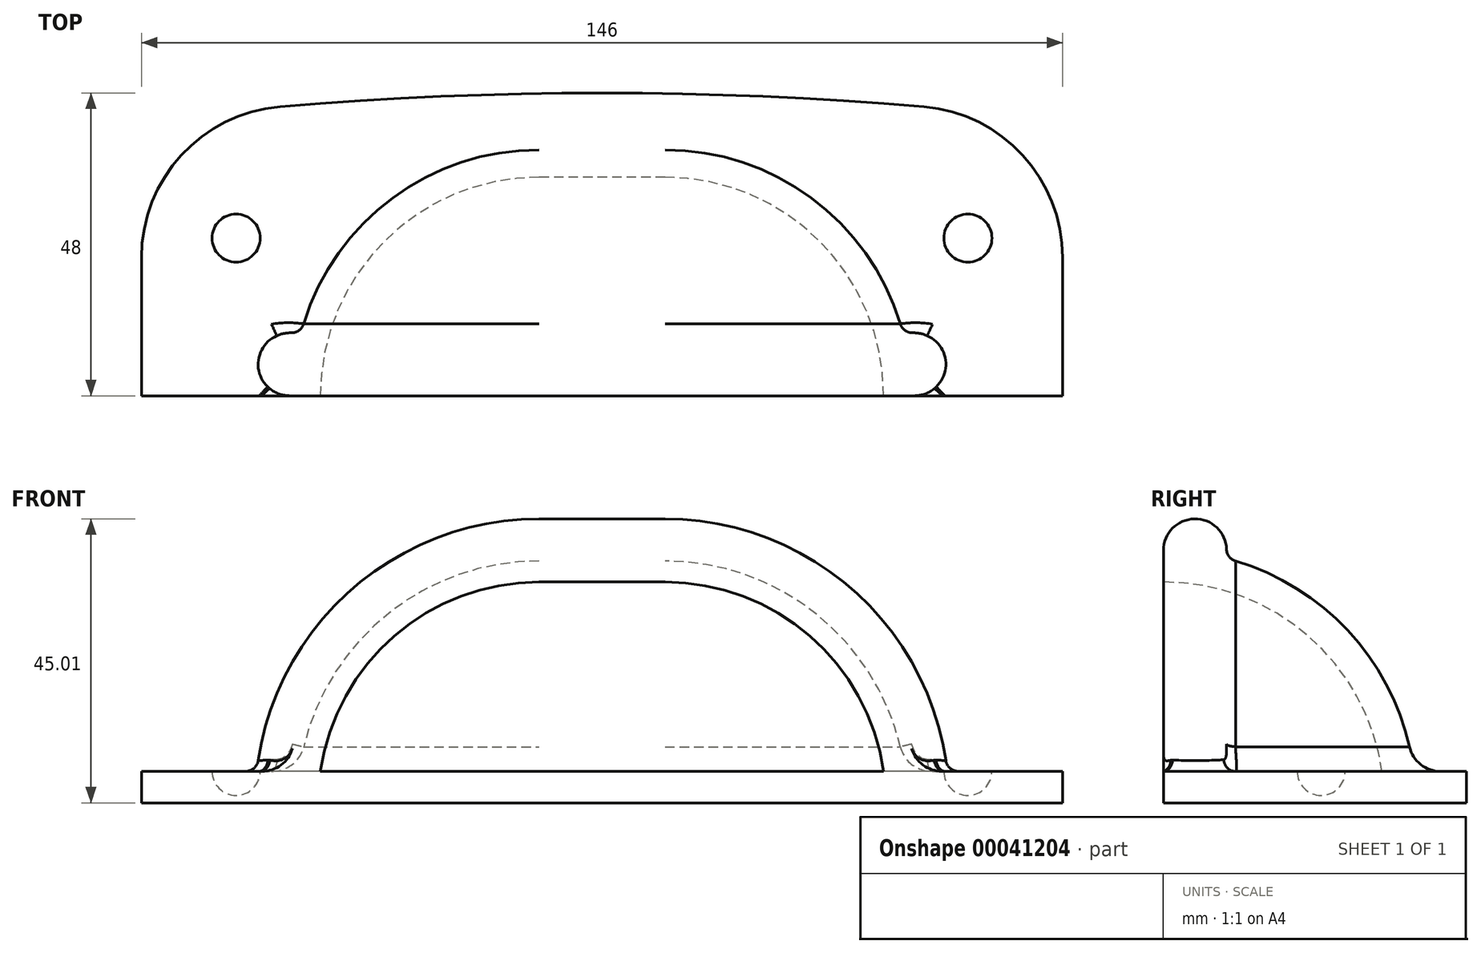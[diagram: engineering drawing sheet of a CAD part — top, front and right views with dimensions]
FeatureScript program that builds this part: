
annotation { "Feature Type Name" : "Feature", "Feature Type Description" : "" }
export const myFeature = defineFeature(function(context is Context, id is Id, definition is map)
    precondition{}
    {
        {
            var Q0;
            Q0=qCreatedBy(makeId("Top.planeOp"),FACE);
            var sketch = newSketch(context, id + "F0", { "sketchPlane" : qUnion([Q0])});
            skLineSegment(sketch, "E0", {"start": v(0, 0) * mm, "end": v(10, 0) * mm, "construction": true});
            skArc(sketch, "E1", {"start": v(10, 35) * mm, "mid": v(34.75, 24.75) * mm, "end": v(45, 0) * mm});
            skLineSegment(sketch, "E2", {"start": v(10, 35) * mm, "end": v(0, 35) * mm});
            skLineSegment(sketch, "E3", {"start": v(45, 0) * mm, "end": v(50, 0) * mm});
            skLineSegment(sketch, "E4.0", {"start": v(10, 40) * mm, "end": v(0, 40) * mm});
            skArc(sketch, "E4.1", {"start": v(10, 40) * mm, "mid": v(38.28, 28.28) * mm, "end": v(50, 0) * mm});
            skLineSegment(sketch, "E5", {"start": v(0, 40) * mm, "end": v(0, 0) * mm, "construction": true});
            skLineSegment(sketch, "E6.MirrorCS", {"start": v(-10, 35) * mm, "end": v(0, 35) * mm});
            skArc(sketch, "E7.MirrorCS", {"start": v(-10, 35) * mm, "mid": v(-34.75, 24.75) * mm, "end": v(-45, 0) * mm});
            skLineSegment(sketch, "E8.MirrorCS", {"start": v(-45, 0) * mm, "end": v(-50, 0) * mm});
            skArc(sketch, "E9.MirrorCS", {"start": v(-10, 40) * mm, "mid": v(-38.28, 28.28) * mm, "end": v(-50, 0) * mm});
            skLineSegment(sketch, "E10.MirrorCS", {"start": v(-10, 40) * mm, "end": v(0, 40) * mm});
            skLineSegment(sketch, "E11.MirrorCS", {"start": v(0, 0) * mm, "end": v(-10, 0) * mm});
            skSolve(sketch);
        }
        {
            var Q0;
            Q0 = qSketchRegion(id + "F0", true);
            var Q1;
            Q1=sQuery(id+"F0.wireOp",EDGE,"E0");
            revolve(context, id + "F1", {"entities" : qUnion([Q0]), "axis" : qUnion([Q1]), "revolveType" : RevolveType.ONE_DIRECTION, "angle" : 90 * degree});
        }
        {
            var Q0;
            Q0=qCreatedBy(makeId("Top.planeOp"),FACE);
            var sketch = newSketch(context, id + "F2", { "sketchPlane" : qUnion([Q0])});
            skArc(sketch, "E12", {"start": v(51.04, 45.83) * mm, "mid": v(25.54, 47.46) * mm, "end": v(0, 48) * mm});
            skLineSegment(sketch, "E13", {"start": v(0, 0) * mm, "end": v(0, 48) * mm, "construction": true});
            skLineSegment(sketch, "E14", {"start": v(0, 48) * mm, "end": v(-79.99, 48) * mm, "construction": true});
            skLineSegment(sketch, "E15", {"start": v(0, 0) * mm, "end": v(10, 0) * mm});
            skLineSegment(sketch, "E16", {"start": v(73, 0) * mm, "end": v(73, 21.91) * mm});
            skPoint(sketch, "E17.visualSharp", {"position": v(73, 43.54) * mm});
            skArc(sketch, "E17.filletArc", {"start": v(73, 21.91) * mm, "mid": v(66.68, 38.14) * mm, "end": v(51.04, 45.83) * mm});
            skArc(sketch, "E18.MirrorCS", {"start": v(-51.04, 45.83) * mm, "mid": v(-25.54, 47.46) * mm, "end": v(0, 48) * mm});
            skArc(sketch, "E19.MirrorCS", {"start": v(-73, 21.91) * mm, "mid": v(-66.68, 38.14) * mm, "end": v(-51.04, 45.83) * mm});
            skLineSegment(sketch, "E20.MirrorCS", {"start": v(-73, 0) * mm, "end": v(-73, 21.91) * mm});
            skLineSegment(sketch, "E21.MirrorCS", {"start": v(0, 0) * mm, "end": v(-10, 0) * mm});
            skArc(sketch, "E22.0", {"start": v(-10, 35) * mm, "mid": v(-34.75, 24.75) * mm, "end": v(-45, 0) * mm});
            skLineSegment(sketch, "E22.1", {"start": v(10, 35) * mm, "end": v(-10, 35) * mm});
            skArc(sketch, "E22.2", {"start": v(10, 35) * mm, "mid": v(34.75, 24.75) * mm, "end": v(45, 0) * mm});
            skLineSegment(sketch, "E23.trimOffspring", {"start": v(-45, 0) * mm, "end": v(-73, 0) * mm});
            skLineSegment(sketch, "E24.trimOffspring", {"start": v(45, 0) * mm, "end": v(73, 0) * mm});
            skSolve(sketch);
        }
        {
            var Q0;
            Q0 = qSketchRegion(id + "F2", true);
            extrude(context, id + "F3", {"entities" : qUnion([Q0]), "operationType" : NewBodyOperationType.ADD, "depth" : 5 * mm});
        }
        {
            var Q0;
            Q0=qCreatedBy(makeId("Right.planeOp"),FACE);
            var sketch = newSketch(context, id + "F4", { "sketchPlane" : qUnion([Q0])});
            skArc(sketch, "E25.0.0", {"start": v(10, 33.54) * mm, "mid": v(5.05, 34.63) * mm, "end": v(0, 35) * mm});
            skArc(sketch, "E25.0.2", {"start": v(0, 35) * mm, "mid": v(5.05, 34.63) * mm, "end": v(10, 33.54) * mm});
            skLineSegment(sketch, "E26", {"start": v(0, 35) * mm, "end": v(0, 40) * mm});
            skArc(sketch, "E27", {"start": v(0, 40) * mm, "mid": v(5, 45) * mm, "end": v(10, 40) * mm});
            skLineSegment(sketch, "E28", {"start": v(10, 40) * mm, "end": v(10, 33.54) * mm});
            skPoint(sketch, "E29.orphan", {"position": v(35, 0) * mm});
            skSolve(sketch);
        }
        {
            var Q0;
            Q0=makeQuery(id+"F3.boolean.opBoolean","MERGE",FACE,{"derivedFrom":[makeQuery(id+"F1.opRevolve","CAP_FACE",FACE,{"disambiguationData":[OSD([sQuery(id+"F0.wireOp",EDGE,"E1"),sQuery(id+"F0.wireOp",EDGE,"E2"),sQuery(id+"F0.wireOp",EDGE,"E3"),sQuery(id+"F0.wireOp",EDGE,"E4.0"),sQuery(id+"F0.wireOp",EDGE,"E4.1"),sQuery(id+"F0.wireOp",EDGE,"E6.MirrorCS"),sQuery(id+"F0.wireOp",EDGE,"E7.MirrorCS"),sQuery(id+"F0.wireOp",EDGE,"E8.MirrorCS"),sQuery(id+"F0.wireOp",EDGE,"E9.MirrorCS"),sQuery(id+"F0.wireOp",EDGE,"E10.MirrorCS")])],"isStart":false}),makeQuery(id+"F3.opExtrude","SWEPT_FACE",FACE,{"disambiguationData":[OSD([sQuery(id+"F2.wireOp",EDGE,"E23.trimOffspring")])]}),makeQuery(id+"F3.opExtrude","SWEPT_FACE",FACE,{"disambiguationData":[OSD([sQuery(id+"F2.wireOp",EDGE,"E24.trimOffspring")])]})]});
            var sketch = newSketch(context, id + "F5", { "sketchPlane" : qUnion([Q0])});
            skLineSegment(sketch, "E30.0", {"start": v(10, 35) * mm, "end": v(0, 35) * mm});
            skArc(sketch, "E30.1", {"start": v(10, 35) * mm, "mid": v(34.75, 24.75) * mm, "end": v(45, 0) * mm});
            skLineSegment(sketch, "E31", {"start": v(0, 0) * mm, "end": v(0, 35) * mm, "construction": true});
            skPoint(sketch, "E32.orphan", {"position": v(-10, 35) * mm});
            skSolve(sketch);
        }
        {
            var Q0;
            Q0 = qSketchRegion(id + "F4", true);
            var Q1;
            Q1 = qConstructionFilter(qBodyType(qCreatedBy(id + "F5" ,EDGE), BodyType.WIRE), ConstructionObject.NO);
            sweep(context, id + "F6", {"profiles" : qUnion([Q0]), "path" : qUnion([Q1])});
        }
        {
            var Q0;
            Q0=makeQuery(id+"F3.boolean.opBoolean","INTERSECT",EDGE,{"derivedFrom":[makeQuery(id+"F1.opRevolve","SWEPT_FACE",FACE,{"disambiguationData":[OSD([sQuery(id+"F0.wireOp",EDGE,"E9.MirrorCS")])]}),makeQuery(id+"F3.opExtrude","CAP_FACE",FACE,{"disambiguationData":[OSD([sQuery(id+"F2.wireOp",EDGE,"E12"),sQuery(id+"F2.wireOp",EDGE,"E15"),sQuery(id+"F2.wireOp",EDGE,"E16"),sQuery(id+"F2.wireOp",EDGE,"E17.filletArc"),sQuery(id+"F2.wireOp",EDGE,"E18.MirrorCS"),sQuery(id+"F2.wireOp",EDGE,"E19.MirrorCS"),sQuery(id+"F2.wireOp",EDGE,"E20.MirrorCS"),sQuery(id+"F2.wireOp",EDGE,"E21.MirrorCS")])],"isStart":false})]});
            fillet(context, id + "F7", {"entities" : qUnion([Q0]), "radius" : 5 * mm, "tangentPropagation" : true, "allowEdgeOverflow" : false});
        }
        {
            var Q0;
            Q0=makeQuery(id+"F6.opSweep","SWEPT_BODY",BODY,{"disambiguationData":[OSD([sQuery(id+"F4.wireOp",EDGE,"E25.0.2"),sQuery(id+"F4.wireOp",EDGE,"E26"),sQuery(id+"F4.wireOp",EDGE,"E27"),sQuery(id+"F4.wireOp",EDGE,"E28"),sQuery(id+"F5.wireOp",EDGE,"E30.1")])]});
            var Q1;
            Q1=qCreatedBy(makeId("Right.planeOp"),FACE);
            mirror(context, id + "F8", {"entities" : qUnion([Q0]), "mirrorPlane" : qUnion([Q1])});
        }
        {
            var Q0;
            Q0=makeQuery(id+"F1.opRevolve","SWEPT_BODY",BODY,{"disambiguationData":[OSD([sQuery(id+"F0.wireOp",EDGE,"E1"),sQuery(id+"F0.wireOp",EDGE,"E2"),sQuery(id+"F0.wireOp",EDGE,"E3"),sQuery(id+"F0.wireOp",EDGE,"E4.0"),sQuery(id+"F0.wireOp",EDGE,"E4.1"),sQuery(id+"F0.wireOp",EDGE,"E6.MirrorCS"),sQuery(id+"F0.wireOp",EDGE,"E7.MirrorCS"),sQuery(id+"F0.wireOp",EDGE,"E8.MirrorCS"),sQuery(id+"F0.wireOp",EDGE,"E9.MirrorCS"),sQuery(id+"F0.wireOp",EDGE,"E10.MirrorCS")])]});
            var Q1;
            Q1=makeQuery(id+"F8.opPattern","COPY",BODY,{"derivedFrom":makeQuery(id+"F6.opSweep","SWEPT_BODY",BODY,{"disambiguationData":[OSD([sQuery(id+"F4.wireOp",EDGE,"E25.0.2"),sQuery(id+"F4.wireOp",EDGE,"E26"),sQuery(id+"F4.wireOp",EDGE,"E27"),sQuery(id+"F4.wireOp",EDGE,"E28"),sQuery(id+"F5.wireOp",EDGE,"E30.1")])]}),"instanceName":"1"});
            var Q2;
            Q2=makeQuery(id+"F6.opSweep","SWEPT_BODY",BODY,{"disambiguationData":[OSD([sQuery(id+"F4.wireOp",EDGE,"E25.0.2"),sQuery(id+"F4.wireOp",EDGE,"E26"),sQuery(id+"F4.wireOp",EDGE,"E27"),sQuery(id+"F4.wireOp",EDGE,"E28"),sQuery(id+"F5.wireOp",EDGE,"E30.1")])]});
            booleanBodies(context, id + "F9", {"operationType" : BooleanOperationType.UNION, "tools" : qUnion([Q0, Q1, Q2])});
        }
        {
            var Q0;
            Q0=makeQuery(id+"F9.opBoolean","INTERSECT",EDGE,{"derivedFrom":[makeQuery(id+"F6.opSweep","SWEPT_FACE",FACE,{"disambiguationData":[OSD([sQuery(id+"F4.wireOp",EDGE,"E28"),sQuery(id+"F5.wireOp",EDGE,"E30.0")])]}),makeQuery(id+"F1.opRevolve","SWEPT_FACE",FACE,{"disambiguationData":[OSD([sQuery(id+"F0.wireOp",EDGE,"E9.MirrorCS")])]})]});
            var Q1;
            {var subQ0=makeQuery(id+"F6.opSweep","SWEPT_EDGE",EDGE,{"disambiguationData":[OSD([sQuery(id+"F4.wireOp",EDGE,"E27"),sQuery(id+"F4.wireOp",EDGE,"E28"),sQuery(id+"F5.wireOp",EDGE,"E30.0")])]});Q1=makeQuery(id+"F9.opBoolean","MERGE",EDGE,{"derivedFrom":[subQ0,makeQuery(id+"F8.opPattern","COPY",EDGE,{"derivedFrom":subQ0,"instanceName":"1"})]});}
            var Q2;
            Q2=makeQuery(id+"F6.opSweep","SWEPT_EDGE",EDGE,{"disambiguationData":[OSD([sQuery(id+"F4.wireOp",EDGE,"E27"),sQuery(id+"F4.wireOp",EDGE,"E28"),sQuery(id+"F5.wireOp",EDGE,"E30.1")])]});
            var Q3;
            Q3=makeQuery(id+"F9.opBoolean","INTERSECT",EDGE,{"derivedFrom":[makeQuery(id+"F7.opFillet","BLEND_FACE",FACE,{"disambiguationData":[OSD([sQuery(id+"F0.wireOp",EDGE,"E9.MirrorCS"),sQuery(id+"F2.wireOp",EDGE,"E12"),sQuery(id+"F2.wireOp",EDGE,"E16"),sQuery(id+"F2.wireOp",EDGE,"E17.filletArc"),sQuery(id+"F2.wireOp",EDGE,"E18.MirrorCS"),sQuery(id+"F2.wireOp",EDGE,"E19.MirrorCS"),sQuery(id+"F2.wireOp",EDGE,"E20.MirrorCS"),sQuery(id+"F2.wireOp",EDGE,"E22.0"),sQuery(id+"F2.wireOp",EDGE,"E22.1"),sQuery(id+"F2.wireOp",EDGE,"E22.2"),sQuery(id+"F2.wireOp",EDGE,"E23.trimOffspring"),sQuery(id+"F2.wireOp",EDGE,"E24.trimOffspring")])]}),makeQuery(id+"F8.opPattern","COPY",FACE,{"derivedFrom":makeQuery(id+"F6.opSweep","SWEPT_FACE",FACE,{"disambiguationData":[OSD([sQuery(id+"F4.wireOp",EDGE,"E27"),sQuery(id+"F5.wireOp",EDGE,"E30.1")])]}),"instanceName":"1"})]});
            var Q4;
            Q4=makeQuery(id+"F8.opPattern","COPY",EDGE,{"derivedFrom":makeQuery(id+"F6.opSweep","SWEPT_EDGE",EDGE,{"disambiguationData":[OSD([sQuery(id+"F4.wireOp",EDGE,"E27"),sQuery(id+"F4.wireOp",EDGE,"E28"),sQuery(id+"F5.wireOp",EDGE,"E30.1")])]}),"instanceName":"1"});
            var Q5;
            Q5=makeQuery(id+"F9.opBoolean","INTERSECT",EDGE,{"derivedFrom":[makeQuery(id+"F6.opSweep","SWEPT_FACE",FACE,{"disambiguationData":[OSD([sQuery(id+"F4.wireOp",EDGE,"E27"),sQuery(id+"F5.wireOp",EDGE,"E30.1")])]}),makeQuery(id+"F7.opFillet","BLEND_FACE",FACE,{"disambiguationData":[OSD([sQuery(id+"F0.wireOp",EDGE,"E4.1"),sQuery(id+"F2.wireOp",EDGE,"E12"),sQuery(id+"F2.wireOp",EDGE,"E16"),sQuery(id+"F2.wireOp",EDGE,"E17.filletArc"),sQuery(id+"F2.wireOp",EDGE,"E18.MirrorCS"),sQuery(id+"F2.wireOp",EDGE,"E19.MirrorCS"),sQuery(id+"F2.wireOp",EDGE,"E20.MirrorCS"),sQuery(id+"F2.wireOp",EDGE,"E22.0"),sQuery(id+"F2.wireOp",EDGE,"E22.1"),sQuery(id+"F2.wireOp",EDGE,"E22.2"),sQuery(id+"F2.wireOp",EDGE,"E23.trimOffspring"),sQuery(id+"F2.wireOp",EDGE,"E24.trimOffspring")])]})]});
            fillet(context, id + "F10", {"entities" : qUnion([Q0, Q1, Q2, Q3, Q4, Q5]), "radius" : 2 * mm, "tangentPropagation" : true, "allowEdgeOverflow" : false});
        }
        {
            var Q0;
            Q0=makeQuery(id+"F3.opExtrude","CAP_FACE",FACE,{"disambiguationData":[OSD([sQuery(id+"F2.wireOp",EDGE,"E12"),sQuery(id+"F2.wireOp",EDGE,"E16"),sQuery(id+"F2.wireOp",EDGE,"E17.filletArc"),sQuery(id+"F2.wireOp",EDGE,"E18.MirrorCS"),sQuery(id+"F2.wireOp",EDGE,"E19.MirrorCS"),sQuery(id+"F2.wireOp",EDGE,"E20.MirrorCS"),sQuery(id+"F2.wireOp",EDGE,"E22.0"),sQuery(id+"F2.wireOp",EDGE,"E22.1"),sQuery(id+"F2.wireOp",EDGE,"E22.2"),sQuery(id+"F2.wireOp",EDGE,"E23.trimOffspring"),sQuery(id+"F2.wireOp",EDGE,"E24.trimOffspring")])],"isStart":false});
            var sketch = newSketch(context, id + "F11", { "sketchPlane" : qUnion([Q0])});
            skArc(sketch, "E33", {"start": v(58, 21.19) * mm, "mid": v(61.81, 25) * mm, "end": v(58, 28.81) * mm});
            skLineSegment(sketch, "E34", {"start": v(58, 25) * mm, "end": v(58, 37.6) * mm, "construction": true});
            skLineSegment(sketch, "E35", {"start": v(58, 25) * mm, "end": v(58, 28.81) * mm});
            skLineSegment(sketch, "E36", {"start": v(58, 25) * mm, "end": v(58, 21.19) * mm});
            skSolve(sketch);
        }
        {
            var Q0;
            Q0=makeQuery(id+"F11.imprint","IMPRINT",FACE,{"disambiguationData":[TD([[makeQuery(id+"F11.imprint","IMPRINT",EDGE,{"derivedFrom":sQuery(id+"F11.wireOp",EDGE,"E33")}),1.0]])]});
            var Q1;
            Q1=sQuery(id+"F11.wireOp",EDGE,"E34");
            revolve(context, id + "F12", {"entities" : qUnion([Q0]), "axis" : qUnion([Q1]), "revolveType" : RevolveType.FULL});
        }
        {
            var Q0;
            Q0=makeQuery(id+"F12.opRevolve","SWEPT_BODY",BODY,{"disambiguationData":[OSD([sQuery(id+"F11.wireOp",EDGE,"E33"),sQuery(id+"F11.wireOp",EDGE,"E35"),sQuery(id+"F11.wireOp",EDGE,"E36")])]});
            var Q1;
            Q1=qCreatedBy(makeId("Right.planeOp"),FACE);
            mirror(context, id + "F13", {"entities" : qUnion([Q0]), "mirrorPlane" : qUnion([Q1])});
        }
        {
            var Q0;
            Q0=makeQuery(id+"F13.opPattern","COPY",BODY,{"derivedFrom":makeQuery(id+"F12.opRevolve","SWEPT_BODY",BODY,{"disambiguationData":[OSD([sQuery(id+"F11.wireOp",EDGE,"E33"),sQuery(id+"F11.wireOp",EDGE,"E35"),sQuery(id+"F11.wireOp",EDGE,"E36")])]}),"instanceName":"1"});
            var Q1;
            Q1=makeQuery(id+"F12.opRevolve","SWEPT_BODY",BODY,{"disambiguationData":[OSD([sQuery(id+"F11.wireOp",EDGE,"E33"),sQuery(id+"F11.wireOp",EDGE,"E35"),sQuery(id+"F11.wireOp",EDGE,"E36")])]});
            var Q2;
            Q2=makeQuery(id+"F1.opRevolve","SWEPT_BODY",BODY,{"disambiguationData":[OSD([sQuery(id+"F0.wireOp",EDGE,"E1"),sQuery(id+"F0.wireOp",EDGE,"E2"),sQuery(id+"F0.wireOp",EDGE,"E3"),sQuery(id+"F0.wireOp",EDGE,"E4.0"),sQuery(id+"F0.wireOp",EDGE,"E4.1"),sQuery(id+"F0.wireOp",EDGE,"E6.MirrorCS"),sQuery(id+"F0.wireOp",EDGE,"E7.MirrorCS"),sQuery(id+"F0.wireOp",EDGE,"E8.MirrorCS"),sQuery(id+"F0.wireOp",EDGE,"E9.MirrorCS"),sQuery(id+"F0.wireOp",EDGE,"E10.MirrorCS")])]});
            booleanBodies(context, id + "F14", {"operationType" : BooleanOperationType.SUBTRACTION, "tools" : qUnion([Q0, Q1]), "targets" : qUnion([Q2])});
        }
        {
            var Q0;
            Q0=qCreatedBy(makeId("Top.planeOp"),FACE);
            var sketch = newSketch(context, id + "F15", { "sketchPlane" : qUnion([Q0])});
            skArc(sketch, "E37.0", {"start": v(-10, 35) * mm, "mid": v(-34.75, 24.75) * mm, "end": v(-45, 0) * mm});
            skLineSegment(sketch, "E37.1", {"start": v(10, 35) * mm, "end": v(-10, 35) * mm});
            skArc(sketch, "E37.2", {"start": v(10, 35) * mm, "mid": v(34.75, 24.75) * mm, "end": v(45, 0) * mm});
            skLineSegment(sketch, "E38", {"start": v(-45, 0) * mm, "end": v(45, 0) * mm});
            skSolve(sketch);
        }
        {
            var Q0;
            Q0 = qSketchRegion(id + "F15", true);
            extrude(context, id + "F16", {"entities" : qUnion([Q0]), "operationType" : NewBodyOperationType.ADD, "depth" : 5 * mm});
        }
    });
